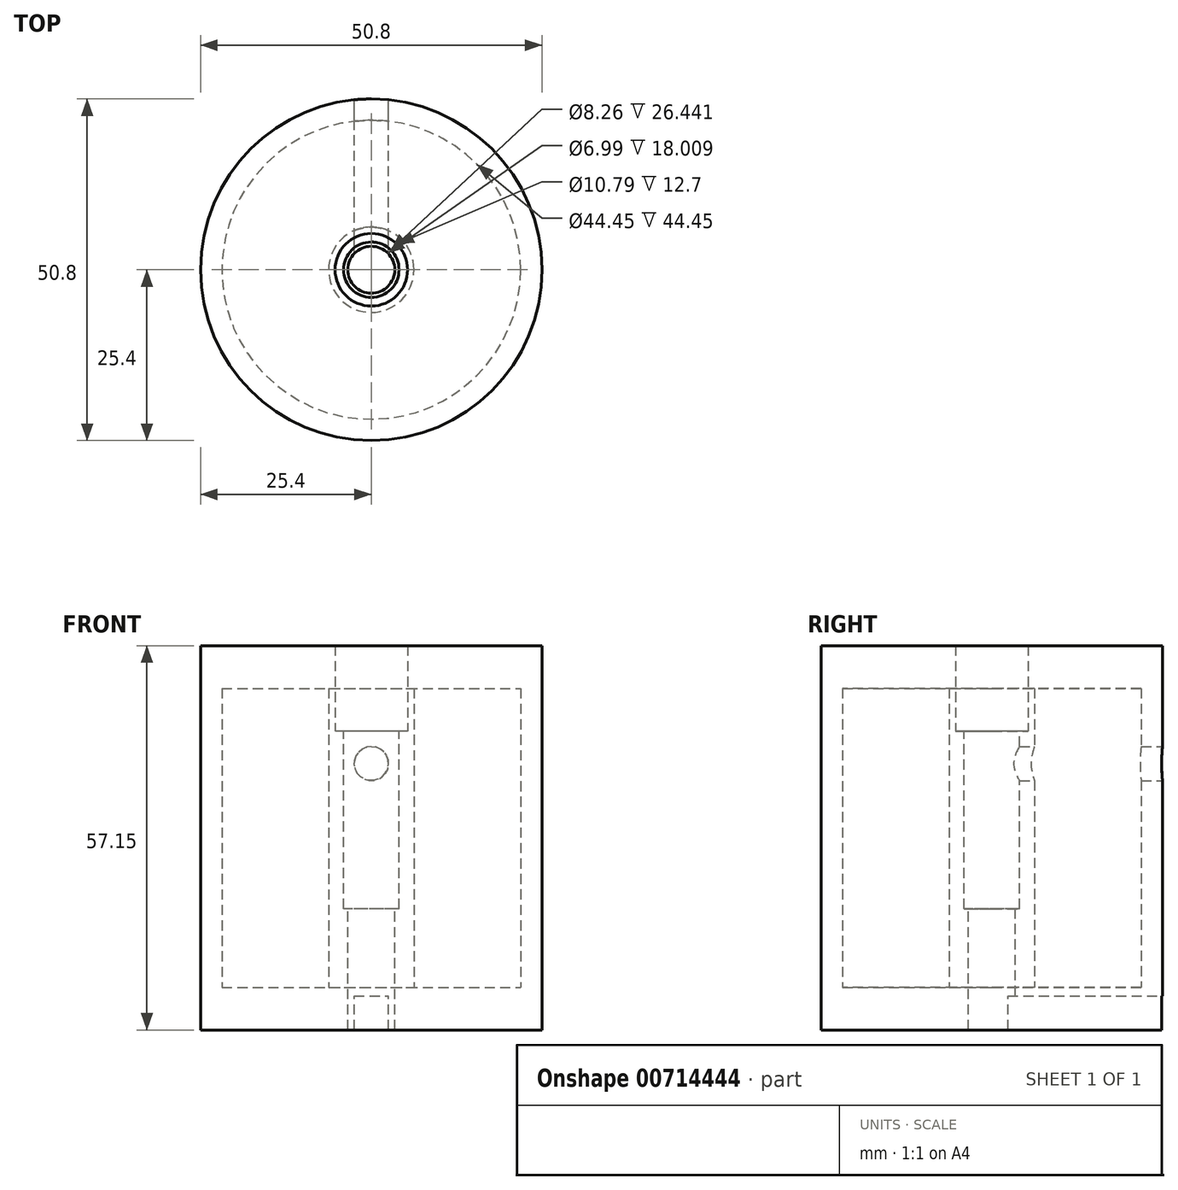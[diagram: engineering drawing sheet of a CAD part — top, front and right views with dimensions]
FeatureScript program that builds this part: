
annotation { "Feature Type Name" : "Feature", "Feature Type Description" : "" }
export const myFeature = defineFeature(function(context is Context, id is Id, definition is map)
    precondition{}
    {
        {
            var Q0;
            Q0=qCreatedBy(makeId("Top.planeOp"),FACE);
            var sketch = newSketch(context, id + "F0", { "sketchPlane" : qUnion([Q0])});
            skCircle(sketch, "E0", {"center": v(0, 0) * mm, "radius": 25.4 * mm});
            skSolve(sketch);
        }
        {
            var Q0;
            Q0=makeQuery(id+"F0.imprint","IMPRINT",FACE,{"disambiguationData":[TD([[makeQuery(id+"F0.imprint","IMPRINT",EDGE,{"derivedFrom":sQuery(id+"F0.wireOp",EDGE,"E0")}),1.0]])]});
            extrude(context, id + "F1", {"entities" : qUnion([Q0]), "oppositeDirection" : true, "depth" : 38.1 * mm});
        }
        {
            var Q0;
            Q0=qCreatedBy(makeId("Front.planeOp"),FACE);
            cPlane(context, id + "F2", {"entities" : qUnion([Q0]), "cplaneType" : CPlaneType.OFFSET, "offset" : 25.4 * mm, "oppositeDirection" : true, "width" : 152.4 * mm, "height" : 152.4 * mm});
        }
        {
            var Q0;
            Q0=makeQuery(id+"F1.opExtrude","CAP_FACE",FACE,{"disambiguationData":[OSD([sQuery(id+"F0.wireOp",EDGE,"E0")])],"isStart":true});
            var sketch = newSketch(context, id + "F3", { "sketchPlane" : qUnion([Q0])});
            skCircle(sketch, "E1", {"center": v(0, 0) * mm, "radius": 4.13 * mm});
            skSolve(sketch);
        }
        {
            var Q0;
            Q0=qSketchRegion(id+"F3",true);
            extrude(context, id + "F4", {"entities" : qUnion([Q0]), "operationType" : NewBodyOperationType.REMOVE, "oppositeDirection" : true, "depth" : 20.1 * mm, "offsetDistance" : 25.4 * mm});
        }
        {
            var Q0;
            Q0=makeQuery(id+"F4.boolean.opBoolean","COPY",FACE,{"derivedFrom":makeQuery(id+"F4.opExtrude","CAP_FACE",FACE,{"disambiguationData":[OSD([sQuery(id+"F3.wireOp",EDGE,"E1")])],"isStart":false})});
            var sketch = newSketch(context, id + "F5", { "sketchPlane" : qUnion([Q0])});
            skCircle(sketch, "E2", {"center": v(0, 0) * mm, "radius": 3.5 * mm});
            skSolve(sketch);
        }
        {
            var Q0;
            Q0=qSketchRegion(id+"F5",true);
            extrude(context, id + "F6", {"entities" : qUnion([Q0]), "operationType" : NewBodyOperationType.REMOVE, "endBound" : BoundingType.THROUGH_ALL, "oppositeDirection" : true, "depth" : 25.4 * mm});
        }
        {
            var Q0;
            Q0=makeQuery(id+"F1.opExtrude","CAP_FACE",FACE,{"disambiguationData":[OSD([sQuery(id+"F0.wireOp",EDGE,"E0")])],"isStart":false});
            var sketch = newSketch(context, id + "F7", { "sketchPlane" : qUnion([Q0])});
            skLineSegment(sketch, "E3.bottom", {"start": v(-2.54, 0) * mm, "end": v(2.54, 0) * mm});
            skLineSegment(sketch, "E3.top", {"start": v(-2.54, -26.67) * mm, "end": v(2.54, -26.67) * mm});
            skLineSegment(sketch, "E3.left", {"start": v(-2.54, 0) * mm, "end": v(-2.54, -26.67) * mm});
            skLineSegment(sketch, "E3.right", {"start": v(2.54, 0) * mm, "end": v(2.54, -26.67) * mm});
            skSolve(sketch);
        }
        {
            var Q0;
            Q0=qSketchRegion(id+"F7",true);
            extrude(context, id + "F8", {"entities" : qUnion([Q0]), "operationType" : NewBodyOperationType.REMOVE, "oppositeDirection" : true, "depth" : 5.08 * mm});
        }
        {
            var Q0;
            Q0=makeQuery(id+"F1.opExtrude","CAP_FACE",FACE,{"disambiguationData":[OSD([sQuery(id+"F0.wireOp",EDGE,"E0")])],"isStart":true});
            var sketch = newSketch(context, id + "F9", { "sketchPlane" : qUnion([Q0])});
            skSolve(sketch);
        }
        {
            var Q0;
            Q0=qSketchRegion(id+"F9",true);
            var Q1;
            Q1=makeQuery(id+"F9.imprint","IMPRINT",FACE,{"disambiguationData":[TD([[makeQuery(id+"F9.imprint","IMPRINT",EDGE,{"derivedFrom":makeQuery(id+"F1.opExtrude","CAP_EDGE",EDGE,{"disambiguationData":[OSD([sQuery(id+"F0.wireOp",EDGE,"E0")])],"isStart":true})}),1.0]])]});
            extrude(context, id + "F10", {"entities" : qUnion([Q0, Q1]), "operationType" : NewBodyOperationType.ADD, "depth" : 6.35 * mm});
        }
        {
            var Q0;
            Q0=makeQuery(id+"F10.opExtrude","CAP_FACE",FACE,{"disambiguationData":[OSD([sQuery(id+"F0.wireOp",EDGE,"E0"),sQuery(id+"F3.wireOp",EDGE,"E1")])],"isStart":false});
            var sketch = newSketch(context, id + "F11", { "sketchPlane" : qUnion([Q0])});
            skCircle(sketch, "E4", {"center": v(0, 0) * mm, "radius": 5.4 * mm});
            skSolve(sketch);
        }
        {
            var Q0;
            Q0=makeQuery(id+"F11.imprint","IMPRINT",FACE,{"disambiguationData":[TD([[makeQuery(id+"F11.imprint","IMPRINT",EDGE,{"derivedFrom":sQuery(id+"F11.wireOp",EDGE,"E4")}),-1.0]])]});
            extrude(context, id + "F12", {"entities" : qUnion([Q0]), "operationType" : NewBodyOperationType.ADD, "depth" : 12.7 * mm});
        }
        {
            var Q0;
            Q0=qCreatedBy(id+"F2.planeOp",FACE);
            var sketch = newSketch(context, id + "F13", { "sketchPlane" : qUnion([Q0])});
            skCircle(sketch, "E5", {"center": v(0, 1.52) * mm, "radius": 2.54 * mm});
            skSolve(sketch);
        }
        {
            var Q0;
            Q0=qSketchRegion(id+"F13",true);
            var Q1;
            Q1=qCreatedBy(makeId("Front.planeOp"),FACE);
            extrude(context, id + "F14", {"entities" : qUnion([Q0]), "operationType" : NewBodyOperationType.REMOVE, "endBound" : BoundingType.UP_TO_SURFACE, "endBoundEntityFace" : qUnion([Q1]), "depth" : 12.7 * mm, "offsetDistance" : 25.4 * mm});
        }
        {
            var Q0;
            {var subQ0=sQuery(id+"F0.wireOp",EDGE,"E0");Q0=makeQuery(id+"FNF6wSeA8XWFWkq_1.boolean.opBoolean","SPLIT",FACE,{"disambiguationData":[TD([makeQuery(id+"F1.opExtrude","SWEPT_FACE",FACE,{"disambiguationData":[OSD([subQ0])]})])],"derivedFrom":makeQuery(id+"F1.opExtrude","CAP_FACE",FACE,{"disambiguationData":[OSD([subQ0])],"isStart":false})});}
            cPlane(context, id + "F15", {"entities" : qUnion([Q0]), "cplaneType" : CPlaneType.OFFSET, "offset" : 6.35 * mm, "oppositeDirection" : true, "width" : 152.4 * mm, "height" : 152.4 * mm});
        }
        {
            var Q0;
            Q0=qCreatedBy(id+"F15.planeOp",FACE);
            var sketch = newSketch(context, id + "F16", { "sketchPlane" : qUnion([Q0])});
            skCircle(sketch, "E6", {"center": v(0, 0) * mm, "radius": 22.23 * mm});
            skCircle(sketch, "E7", {"center": v(0, 0) * mm, "radius": 6.35 * mm});
            skSolve(sketch);
        }
        {
            var Q0;
            Q0 = qSketchRegion(id + "F16", true);
            extrude(context, id + "F17", {"entities" : qUnion([Q0]), "operationType" : NewBodyOperationType.REMOVE, "oppositeDirection" : true, "depth" : 44.45 * mm, "offsetDistance" : 25.4 * mm});
        }
    });
